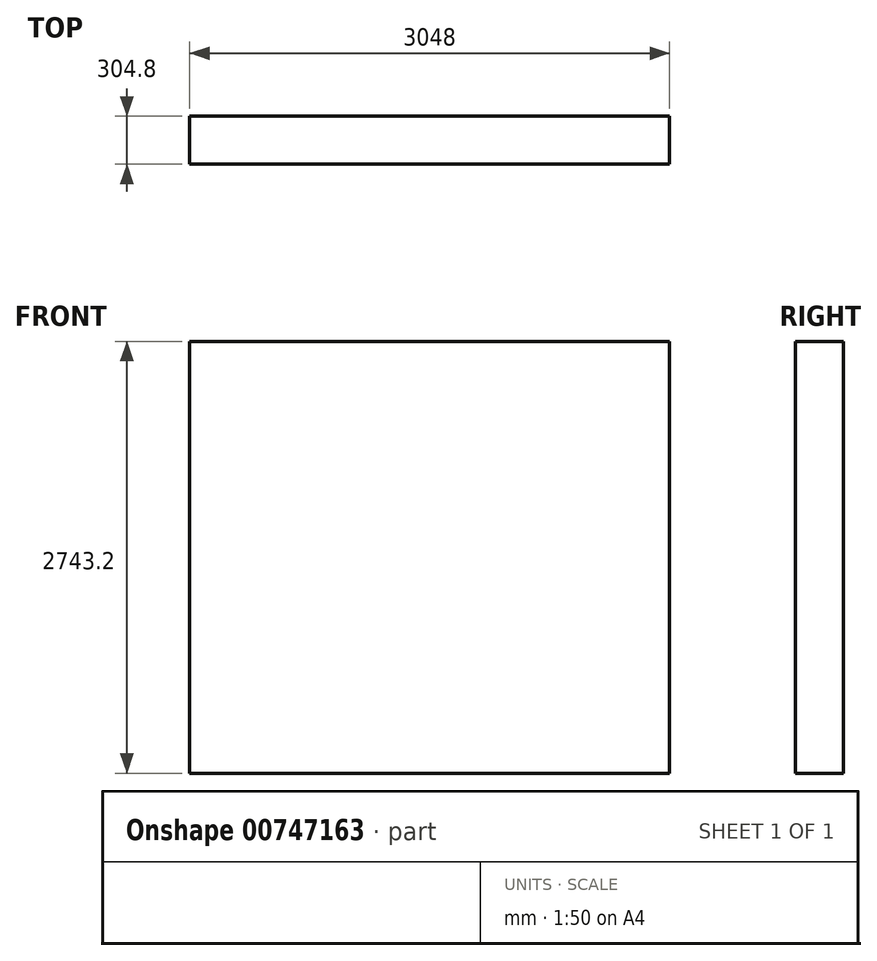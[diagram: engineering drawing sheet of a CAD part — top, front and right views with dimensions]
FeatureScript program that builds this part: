
annotation { "Feature Type Name" : "Feature", "Feature Type Description" : "" }
export const myFeature = defineFeature(function(context is Context, id is Id, definition is map)
    precondition{}
    {
        {
            var Q0;
            Q0=qCreatedBy(makeId("Right.planeOp"),FACE);
            var sketch = newSketch(context, id + "F0", { "sketchPlane" : qUnion([Q0])});
            skLineSegment(sketch, "E0.bottom", {"start": v(-199.8, 1723.3) * mm, "end": v(105, 1723.3) * mm});
            skLineSegment(sketch, "E0.top", {"start": v(-199.8, -1019.9) * mm, "end": v(105, -1019.9) * mm});
            skLineSegment(sketch, "E0.left", {"start": v(-199.8, 1723.3) * mm, "end": v(-199.8, -1019.9) * mm});
            skLineSegment(sketch, "E0.right", {"start": v(105, 1723.3) * mm, "end": v(105, -1019.9) * mm});
            skSolve(sketch);
        }
        {
            var Q0;
            Q0 = qSketchRegion(id + "F0", true);
            extrude(context, id + "F1", {"entities" : qUnion([Q0]), "oppositeDirection" : true, "depth" : 3048 * mm, "offsetDistance" : 25.4 * mm});
        }
    });
